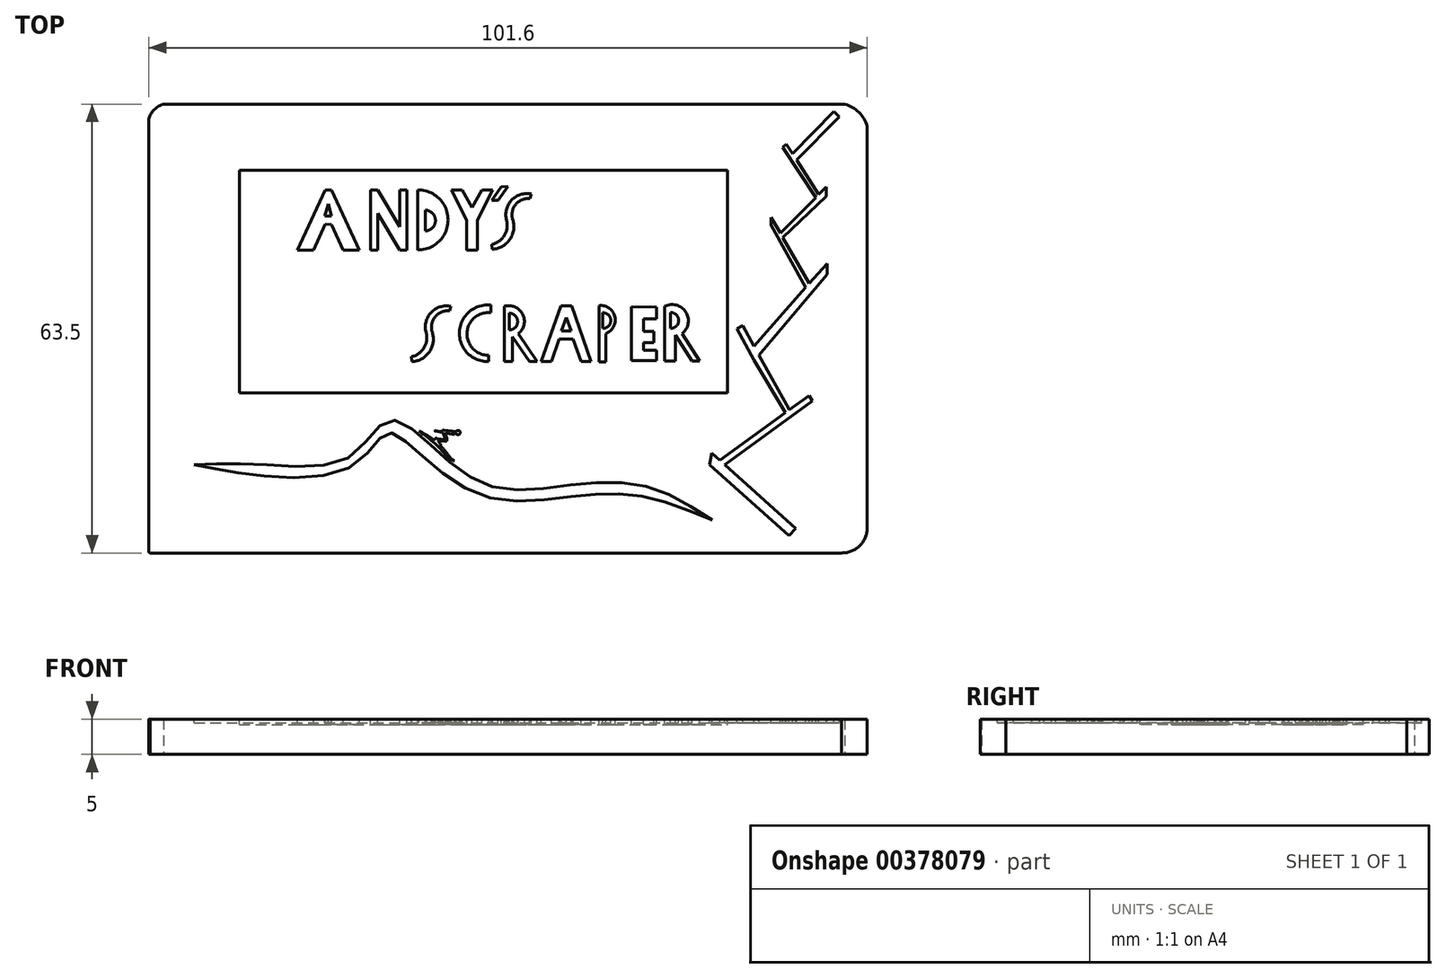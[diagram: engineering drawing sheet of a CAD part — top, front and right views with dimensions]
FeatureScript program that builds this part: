
annotation { "Feature Type Name" : "Feature", "Feature Type Description" : "" }
export const myFeature = defineFeature(function(context is Context, id is Id, definition is map)
    precondition{}
    {
        {
            var Q0;
            Q0=qCreatedBy(makeId("Top.planeOp"),FACE);
            var sketch = newSketch(context, id + "F0", { "sketchPlane" : qUnion([Q0])});
            skLineSegment(sketch, "E0.bottom", {"start": v(2.1, 0) * mm, "end": v(98.44, 0) * mm});
            skLineSegment(sketch, "E0.top", {"start": v(0.18, -63.5) * mm, "end": v(98.16, -63.5) * mm});
            skLineSegment(sketch, "E0.left", {"start": v(0, -2.1) * mm, "end": v(0, -63.32) * mm});
            skLineSegment(sketch, "E0.right", {"start": v(101.6, -3.16) * mm, "end": v(101.6, -60.06) * mm});
            skArc(sketch, "E1", {"start": v(101.6, -3.16) * mm, "mid": v(100.43, -1.17) * mm, "end": v(98.44, 0) * mm});
            skArc(sketch, "E2", {"start": v(2.1, 0) * mm, "mid": v(0.78, -0.78) * mm, "end": v(0, -2.1) * mm});
            skArc(sketch, "E3", {"start": v(98, -63.5) * mm, "mid": v(100.57, -62.47) * mm, "end": v(101.6, -59.9) * mm});
            skArc(sketch, "E4", {"start": v(0, -63.32) * mm, "mid": v(0.05, -63.45) * mm, "end": v(0.18, -63.5) * mm});
            skPoint(sketch, "E5.start.orphan", {"position": v(1.05, -1.05) * mm});
            skSolve(sketch);
        }
        {
            var Q0;
            Q0 = qSketchRegion(id + "F0", true);
            extrude(context, id + "F1", {"entities" : qUnion([Q0]), "depth" : 5 * mm});
        }
        {
            var Q0;
            Q0=makeQuery(id+"F1.opExtrude","CAP_FACE",FACE,{"disambiguationData":[OSD([sQuery(id+"F0.wireOp",EDGE,"E0.bottom"),sQuery(id+"F0.wireOp",EDGE,"E0.top"),sQuery(id+"F0.wireOp",EDGE,"E0.left"),sQuery(id+"F0.wireOp",EDGE,"E0.right"),sQuery(id+"F0.wireOp",EDGE,"E1"),sQuery(id+"F0.wireOp",EDGE,"E2"),sQuery(id+"F0.wireOp",EDGE,"E3"),sQuery(id+"F0.wireOp",EDGE,"E4")])],"isStart":false});
            var sketch = newSketch(context, id + "F2", { "sketchPlane" : qUnion([Q0])});
            skLineSegment(sketch, "E6", {"start": v(21.04, -20.64) * mm, "end": v(23.28, -20.64) * mm});
            skLineSegment(sketch, "E7", {"start": v(23.28, -20.64) * mm, "end": v(24.96, -17) * mm});
            skLineSegment(sketch, "E8", {"start": v(21.04, -20.64) * mm, "end": v(24.96, -12.15) * mm});
            skLineSegment(sketch, "E9", {"start": v(24.9, -15.5) * mm, "end": v(25.4, -15.5) * mm});
            skLineSegment(sketch, "E10", {"start": v(24.9, -15.5) * mm, "end": v(25.4, -13.88) * mm});
            skLineSegment(sketch, "E11.MirrorCS", {"start": v(29.76, -20.69) * mm, "end": v(25.84, -12.15) * mm});
            skLineSegment(sketch, "E12.MirrorCS", {"start": v(27.52, -20.69) * mm, "end": v(25.84, -17.05) * mm});
            skLineSegment(sketch, "E13.MirrorCS", {"start": v(29.76, -20.69) * mm, "end": v(27.52, -20.69) * mm});
            skLineSegment(sketch, "E14.MirrorCS", {"start": v(25.9, -15.5) * mm, "end": v(25.4, -15.5) * mm});
            skLineSegment(sketch, "E15.MirrorCS", {"start": v(25.9, -15.5) * mm, "end": v(25.4, -13.88) * mm});
            skLineSegment(sketch, "E16", {"start": v(31.39, -20.69) * mm, "end": v(31.39, -12.15) * mm});
            skLineSegment(sketch, "E17", {"start": v(31.39, -12.15) * mm, "end": v(32.4, -12.15) * mm});
            skLineSegment(sketch, "E18", {"start": v(36.53, -20.69) * mm, "end": v(35.52, -20.69) * mm});
            skLineSegment(sketch, "E19", {"start": v(32.4, -15.46) * mm, "end": v(32.4, -20.69) * mm});
            skLineSegment(sketch, "E20", {"start": v(32.4, -20.69) * mm, "end": v(31.39, -20.69) * mm});
            skLineSegment(sketch, "E21", {"start": v(35.52, -20.69) * mm, "end": v(36.53, -20.69) * mm});
            skLineSegment(sketch, "E22", {"start": v(36.53, -12.15) * mm, "end": v(36.53, -20.69) * mm});
            skLineSegment(sketch, "E23", {"start": v(36.53, -12.15) * mm, "end": v(35.52, -12.15) * mm});
            skLineSegment(sketch, "E24", {"start": v(35.52, -12.15) * mm, "end": v(35.52, -17.35) * mm});
            skLineSegment(sketch, "E25", {"start": v(32.4, -12.15) * mm, "end": v(35.52, -17.35) * mm});
            skLineSegment(sketch, "E26", {"start": v(32.4, -15.46) * mm, "end": v(35.52, -20.69) * mm});
            skLineSegment(sketch, "E27", {"start": v(38.03, -12.15) * mm, "end": v(38.03, -20.64) * mm});
            skArc(sketch, "E28", {"start": v(38.03, -20.64) * mm, "mid": v(42.33, -16.4) * mm, "end": v(38.03, -12.15) * mm});
            skPoint(sketch, "E29.endSnap0", {"position": v(42.33, -16.4) * mm});
            skLineSegment(sketch, "E30", {"start": v(39.14, -16.42) * mm, "end": v(39.14, -17.62) * mm});
            skLineSegment(sketch, "E31.MirrorCS", {"start": v(39.14, -16.42) * mm, "end": v(39.14, -15.22) * mm});
            skArc(sketch, "E32", {"start": v(39.14, -17.62) * mm, "mid": v(40.36, -16.42) * mm, "end": v(39.14, -15.22) * mm});
            skLineSegment(sketch, "E33", {"start": v(42.77, -12.15) * mm, "end": v(44.93, -16.4) * mm});
            skLineSegment(sketch, "E34", {"start": v(44.93, -16.4) * mm, "end": v(44.93, -20.64) * mm});
            skLineSegment(sketch, "E35", {"start": v(42.77, -12.15) * mm, "end": v(44.3, -12.15) * mm});
            skLineSegment(sketch, "E36", {"start": v(44.3, -12.15) * mm, "end": v(45.7, -14.62) * mm});
            skLineSegment(sketch, "E37.MirrorCS", {"start": v(46.45, -16.4) * mm, "end": v(46.45, -20.64) * mm});
            skLineSegment(sketch, "E38", {"start": v(44.93, -20.64) * mm, "end": v(46.45, -20.64) * mm});
            skLineSegment(sketch, "E39.MirrorCS", {"start": v(47.1, -12.15) * mm, "end": v(45.7, -14.62) * mm});
            skLineSegment(sketch, "E40.MirrorCS", {"start": v(48.62, -12.15) * mm, "end": v(47.1, -12.15) * mm});
            skLineSegment(sketch, "E41.MirrorCS", {"start": v(48.62, -12.15) * mm, "end": v(46.45, -16.4) * mm});
            skPoint(sketch, "E42.endSnap0", {"position": v(36.02, -20.69) * mm});
            skLineSegment(sketch, "E43", {"start": v(49.84, -11.7) * mm, "end": v(48.5, -13.62) * mm});
            skLineSegment(sketch, "E44", {"start": v(48.5, -13.62) * mm, "end": v(49.4, -13.62) * mm});
            skLineSegment(sketch, "E45", {"start": v(49.4, -13.62) * mm, "end": v(50.79, -11.65) * mm});
            skLineSegment(sketch, "E46", {"start": v(50.79, -11.65) * mm, "end": v(49.84, -11.7) * mm});
            skArc(sketch, "E47", {"start": v(54.1, -12.73) * mm, "mid": v(51.32, -13.59) * mm, "end": v(50.6, -16.4) * mm});
            skArc(sketch, "E48", {"start": v(53.93, -13.36) * mm, "mid": v(51.88, -14.21) * mm, "end": v(51.48, -16.4) * mm});
            skLineSegment(sketch, "E49", {"start": v(54.1, -12.73) * mm, "end": v(53.93, -13.36) * mm});
            skArc(sketch, "E50", {"start": v(48.6, -20.53) * mm, "mid": v(51.06, -19.17) * mm, "end": v(51.48, -16.4) * mm});
            skArc(sketch, "E51", {"start": v(48.53, -19.85) * mm, "mid": v(50.3, -18.57) * mm, "end": v(50.6, -16.4) * mm});
            skLineSegment(sketch, "E52", {"start": v(48.53, -19.85) * mm, "end": v(48.6, -20.53) * mm});
            skArc(sketch, "E53.MirrorCS", {"start": v(42.7, -28.62) * mm, "mid": v(39.94, -29.48) * mm, "end": v(39.22, -32.3) * mm});
            skArc(sketch, "E54.MirrorCS", {"start": v(42.54, -29.25) * mm, "mid": v(40.5, -30.1) * mm, "end": v(40.1, -32.3) * mm});
            skArc(sketch, "E55.MirrorCS", {"start": v(37.22, -36.44) * mm, "mid": v(39.68, -35.07) * mm, "end": v(40.1, -32.3) * mm});
            skArc(sketch, "E56.MirrorCS", {"start": v(37.15, -35.75) * mm, "mid": v(38.93, -34.47) * mm, "end": v(39.22, -32.3) * mm});
            skLineSegment(sketch, "E57.MirrorCS", {"start": v(42.7, -28.62) * mm, "end": v(42.54, -29.25) * mm});
            skLineSegment(sketch, "E58.MirrorCS", {"start": v(37.15, -35.75) * mm, "end": v(37.22, -36.44) * mm});
            skArc(sketch, "E59", {"start": v(48.4, -28.45) * mm, "mid": v(43.93, -32.27) * mm, "end": v(48.08, -36.44) * mm});
            skLineSegment(sketch, "E60", {"start": v(48.08, -36.44) * mm, "end": v(48.08, -35.54) * mm});
            skLineSegment(sketch, "E61", {"start": v(48.4, -28.45) * mm, "end": v(48.4, -29.53) * mm});
            skArc(sketch, "E62", {"start": v(48.4, -29.53) * mm, "mid": v(45.01, -32.36) * mm, "end": v(48.08, -35.54) * mm});
            skLineSegment(sketch, "E63", {"start": v(50.26, -28.62) * mm, "end": v(50.26, -36.44) * mm});
            skLineSegment(sketch, "E64", {"start": v(50.26, -36.44) * mm, "end": v(51.42, -36.44) * mm});
            skLineSegment(sketch, "E65", {"start": v(51.42, -36.44) * mm, "end": v(51.42, -32.9) * mm});
            skLineSegment(sketch, "E66", {"start": v(51.42, -32.9) * mm, "end": v(53.87, -36.44) * mm});
            skLineSegment(sketch, "E67", {"start": v(53.87, -36.44) * mm, "end": v(54.92, -36.44) * mm});
            skArc(sketch, "E68", {"start": v(51.42, -32.09) * mm, "mid": v(52.45, -30.92) * mm, "end": v(51.42, -29.75) * mm});
            skLineSegment(sketch, "E69", {"start": v(51.42, -29.75) * mm, "end": v(51.42, -32.09) * mm});
            skArc(sketch, "E70", {"start": v(52.26, -32.5) * mm, "mid": v(52.88, -29.73) * mm, "end": v(50.26, -28.62) * mm});
            skLineSegment(sketch, "E71", {"start": v(54.92, -36.44) * mm, "end": v(52.26, -32.5) * mm});
            skLineSegment(sketch, "E72", {"start": v(55.52, -36.44) * mm, "end": v(58.29, -28.57) * mm});
            skLineSegment(sketch, "E73", {"start": v(58.29, -28.57) * mm, "end": v(59.05, -28.57) * mm});
            skLineSegment(sketch, "E74", {"start": v(55.52, -36.44) * mm, "end": v(56.94, -36.44) * mm});
            skLineSegment(sketch, "E75", {"start": v(56.94, -36.44) * mm, "end": v(58.06, -33.23) * mm});
            skLineSegment(sketch, "E76", {"start": v(59.05, -30.1) * mm, "end": v(58.5, -32.04) * mm});
            skLineSegment(sketch, "E77.MirrorCS", {"start": v(59.05, -30.1) * mm, "end": v(59.6, -32.04) * mm});
            skLineSegment(sketch, "E78.MirrorCS", {"start": v(59.8, -28.57) * mm, "end": v(59.05, -28.57) * mm});
            skLineSegment(sketch, "E79.MirrorCS", {"start": v(62.58, -36.44) * mm, "end": v(59.8, -28.57) * mm});
            skLineSegment(sketch, "E80.MirrorCS", {"start": v(61.16, -36.44) * mm, "end": v(60.03, -33.23) * mm});
            skLineSegment(sketch, "E81.MirrorCS", {"start": v(62.58, -36.44) * mm, "end": v(61.16, -36.44) * mm});
            skLineSegment(sketch, "E82", {"start": v(58.5, -32.04) * mm, "end": v(59.6, -32.04) * mm});
            skLineSegment(sketch, "E83", {"start": v(60.03, -33.23) * mm, "end": v(58.06, -33.23) * mm});
            skLineSegment(sketch, "E84", {"start": v(63.7, -36.45) * mm, "end": v(63.7, -28.52) * mm});
            skLineSegment(sketch, "E85", {"start": v(63.7, -36.45) * mm, "end": v(64.62, -36.45) * mm});
            skLineSegment(sketch, "E86", {"start": v(64.62, -36.45) * mm, "end": v(64.62, -32.46) * mm});
            skArc(sketch, "E87", {"start": v(64.62, -32.46) * mm, "mid": v(65.91, -30.08) * mm, "end": v(63.7, -28.52) * mm});
            skLineSegment(sketch, "E88", {"start": v(64.49, -31.5) * mm, "end": v(64.49, -29.7) * mm});
            skArc(sketch, "E89", {"start": v(64.49, -31.5) * mm, "mid": v(65.17, -30.6) * mm, "end": v(64.49, -29.7) * mm});
            skLineSegment(sketch, "E90", {"start": v(68.27, -28.69) * mm, "end": v(68.27, -36.28) * mm});
            skLineSegment(sketch, "E91", {"start": v(68.27, -36.28) * mm, "end": v(71.83, -36.28) * mm});
            skLineSegment(sketch, "E92", {"start": v(71.83, -36.28) * mm, "end": v(71.83, -34.86) * mm});
            skLineSegment(sketch, "E93", {"start": v(71.83, -34.86) * mm, "end": v(69.95, -34.86) * mm});
            skLineSegment(sketch, "E94", {"start": v(69.95, -34.86) * mm, "end": v(69.95, -33.72) * mm});
            skLineSegment(sketch, "E95", {"start": v(69.95, -33.72) * mm, "end": v(71.41, -33.72) * mm});
            skLineSegment(sketch, "E96", {"start": v(71.41, -33.72) * mm, "end": v(71.41, -32.17) * mm});
            skLineSegment(sketch, "E97", {"start": v(71.41, -32.17) * mm, "end": v(69.99, -32.17) * mm});
            skLineSegment(sketch, "E98", {"start": v(69.99, -32.17) * mm, "end": v(69.99, -30.36) * mm});
            skLineSegment(sketch, "E99", {"start": v(69.99, -30.36) * mm, "end": v(71.83, -30.36) * mm});
            skLineSegment(sketch, "E100", {"start": v(71.83, -30.36) * mm, "end": v(71.83, -28.73) * mm});
            skLineSegment(sketch, "E101", {"start": v(71.83, -28.73) * mm, "end": v(68.27, -28.69) * mm});
            skLineSegment(sketch, "E102", {"start": v(72.96, -36.35) * mm, "end": v(72.96, -28.62) * mm});
            skLineSegment(sketch, "E103", {"start": v(72.96, -36.35) * mm, "end": v(74.5, -36.35) * mm});
            skLineSegment(sketch, "E104", {"start": v(74.5, -36.35) * mm, "end": v(74.5, -32.67) * mm});
            skLineSegment(sketch, "E105", {"start": v(74.5, -32.67) * mm, "end": v(76.82, -36.35) * mm});
            skLineSegment(sketch, "E106", {"start": v(76.82, -36.35) * mm, "end": v(77.91, -36.35) * mm});
            skLineSegment(sketch, "E107", {"start": v(77.91, -36.35) * mm, "end": v(75.47, -32.47) * mm});
            skArc(sketch, "E108", {"start": v(75.47, -32.47) * mm, "mid": v(75.94, -29.42) * mm, "end": v(72.96, -28.62) * mm});
            skLineSegment(sketch, "E109", {"start": v(73.93, -29.42) * mm, "end": v(73.93, -31.42) * mm});
            skArc(sketch, "E110", {"start": v(73.93, -31.42) * mm, "mid": v(74.93, -30.42) * mm, "end": v(73.93, -29.42) * mm});
            skLineSegment(sketch, "E111.bottom", {"start": v(12.82, -9.34) * mm, "end": v(81.83, -9.34) * mm});
            skLineSegment(sketch, "E111.top", {"start": v(12.82, -40.88) * mm, "end": v(81.83, -40.88) * mm});
            skLineSegment(sketch, "E111.left", {"start": v(12.82, -9.34) * mm, "end": v(12.82, -40.88) * mm});
            skLineSegment(sketch, "E111.right", {"start": v(81.83, -9.34) * mm, "end": v(81.83, -40.88) * mm});
            skLineSegment(sketch, "E112", {"start": v(24.96, -17) * mm, "end": v(25.84, -17.05) * mm});
            skLineSegment(sketch, "E113", {"start": v(24.96, -12.15) * mm, "end": v(25.84, -12.15) * mm});
            skSolve(sketch);
        }
        {
            var Q0;
            Q0=makeQuery(id+"F2.imprint","IMPRINT",FACE,{"disambiguationData":[TD([[makeQuery(id+"F2.imprint","IMPRINT",EDGE,{"derivedFrom":sQuery(id+"F2.wireOp",EDGE,"E6")}),-1.0]])]});
            extrude(context, id + "F3", {"entities" : qUnion([Q0]), "operationType" : NewBodyOperationType.REMOVE, "oppositeDirection" : true, "depth" : 0.76 * mm});
        }
        {
            var Q0;
            {var subQ0=sQuery(id+"F0.wireOp",EDGE,"E0.bottom");var subQ1=sQuery(id+"F0.wireOp",EDGE,"E4");var subQ2=sQuery(id+"F0.wireOp",EDGE,"E3");var subQ3=sQuery(id+"F0.wireOp",EDGE,"E2");var subQ4=sQuery(id+"F0.wireOp",EDGE,"E1");var subQ5=sQuery(id+"F0.wireOp",EDGE,"E0.right");var subQ6=sQuery(id+"F0.wireOp",EDGE,"E0.top");var subQ7=sQuery(id+"F0.wireOp",EDGE,"E0.left");Q0=makeQuery(id+"F3.boolean.opBoolean","SPLIT",FACE,{"disambiguationData":[TD([makeQuery(id+"F1.opExtrude","SWEPT_FACE",FACE,{"disambiguationData":[OSD([subQ0])]})])],"derivedFrom":makeQuery(id+"F1.opExtrude","CAP_FACE",FACE,{"disambiguationData":[OSD([subQ0,subQ6,subQ7,subQ5,subQ4,subQ3,subQ2,subQ1])],"isStart":false})});}
            var sketch = newSketch(context, id + "F4", { "sketchPlane" : qUnion([Q0])});
            skLineSegment(sketch, "E114", {"start": v(25.39, -14.1) * mm, "end": v(24.9, -15.86) * mm});
            skLineSegment(sketch, "E115", {"start": v(24.9, -15.86) * mm, "end": v(25.82, -15.86) * mm});
            skLineSegment(sketch, "E116", {"start": v(25.82, -15.86) * mm, "end": v(25.39, -14.1) * mm});
            skLineSegment(sketch, "E117", {"start": v(39.08, -15.02) * mm, "end": v(39.08, -17.95) * mm});
            skArc(sketch, "E118", {"start": v(39.08, -17.95) * mm, "mid": v(40.55, -16.48) * mm, "end": v(39.08, -15.02) * mm});
            skLineSegment(sketch, "E119", {"start": v(50.97, -29.6) * mm, "end": v(50.97, -31.96) * mm});
            skArc(sketch, "E120", {"start": v(50.97, -31.96) * mm, "mid": v(52.17, -30.77) * mm, "end": v(50.97, -29.6) * mm});
            skLineSegment(sketch, "E121", {"start": v(58.33, -32.1) * mm, "end": v(59.72, -32.13) * mm});
            skLineSegment(sketch, "E122", {"start": v(59.06, -30.18) * mm, "end": v(58.33, -32.1) * mm});
            skLineSegment(sketch, "E123", {"start": v(59.06, -30.18) * mm, "end": v(59.72, -32.13) * mm});
            skLineSegment(sketch, "E124", {"start": v(64.22, -29.52) * mm, "end": v(64.22, -31.73) * mm});
            skArc(sketch, "E125", {"start": v(64.22, -31.73) * mm, "mid": v(65.34, -30.63) * mm, "end": v(64.22, -29.52) * mm});
            skLineSegment(sketch, "E126", {"start": v(73.81, -29.5) * mm, "end": v(73.81, -31.74) * mm});
            skArc(sketch, "E127", {"start": v(73.81, -31.74) * mm, "mid": v(74.96, -30.61) * mm, "end": v(73.81, -29.5) * mm});
            skSolve(sketch);
        }
        {
            var Q0;
            Q0 = qSketchRegion(id + "F4", true);
            extrude(context, id + "F5", {"entities" : qUnion([Q0]), "operationType" : NewBodyOperationType.REMOVE, "oppositeDirection" : true, "depth" : 0.5 * mm});
        }
        {
            var Q0;
            {var subQ0=sQuery(id+"F0.wireOp",EDGE,"E0.bottom");var subQ1=sQuery(id+"F0.wireOp",EDGE,"E4");var subQ2=sQuery(id+"F0.wireOp",EDGE,"E3");var subQ3=sQuery(id+"F0.wireOp",EDGE,"E2");var subQ4=sQuery(id+"F0.wireOp",EDGE,"E1");var subQ5=sQuery(id+"F0.wireOp",EDGE,"E0.right");var subQ6=sQuery(id+"F0.wireOp",EDGE,"E0.top");var subQ7=sQuery(id+"F0.wireOp",EDGE,"E0.left");Q0=makeQuery(id+"F3.boolean.opBoolean","SPLIT",FACE,{"disambiguationData":[TD([makeQuery(id+"F1.opExtrude","SWEPT_FACE",FACE,{"disambiguationData":[OSD([subQ0])]})])],"derivedFrom":makeQuery(id+"F1.opExtrude","CAP_FACE",FACE,{"disambiguationData":[OSD([subQ0,subQ6,subQ7,subQ5,subQ4,subQ3,subQ2,subQ1])],"isStart":false})});}
            var sketch = newSketch(context, id + "F6", { "sketchPlane" : qUnion([Q0])});
            skLineSegment(sketch, "E128", {"start": v(85.59, -36.24) * mm, "end": v(83.2, -31.76) * mm});
            skLineSegment(sketch, "E129", {"start": v(83.2, -31.76) * mm, "end": v(84.02, -31.32) * mm});
            skLineSegment(sketch, "E130", {"start": v(84.02, -31.32) * mm, "end": v(85.59, -34.27) * mm});
            skLineSegment(sketch, "E131", {"start": v(85.59, -34.27) * mm, "end": v(92.92, -25.97) * mm});
            skPoint(sketch, "E131.startSnap0", {"position": v(85.59, -36.24) * mm});
            skLineSegment(sketch, "E132", {"start": v(95.95, -22.55) * mm, "end": v(95.95, -24.1) * mm});
            skLineSegment(sketch, "E133", {"start": v(95.95, -24.1) * mm, "end": v(86.27, -35.55) * mm});
            skLineSegment(sketch, "E134", {"start": v(85.59, -36.24) * mm, "end": v(90.05, -43.66) * mm});
            skLineSegment(sketch, "E135", {"start": v(90.57, -43.13) * mm, "end": v(86.27, -35.55) * mm});
            skLineSegment(sketch, "E136", {"start": v(93.44, -25.39) * mm, "end": v(89.68, -18.9) * mm});
            skLineSegment(sketch, "E137", {"start": v(88, -16.03) * mm, "end": v(88, -17.13) * mm});
            skLineSegment(sketch, "E138", {"start": v(88, -17.13) * mm, "end": v(92.92, -25.97) * mm});
            skLineSegment(sketch, "E139", {"start": v(89.32, -18.28) * mm, "end": v(94.33, -13.24) * mm});
            skLineSegment(sketch, "E140", {"start": v(95.82, -11.74) * mm, "end": v(95.82, -13.05) * mm});
            skLineSegment(sketch, "E141", {"start": v(95.82, -13.05) * mm, "end": v(89.68, -18.9) * mm});
            skLineSegment(sketch, "E142", {"start": v(94.74, -12.82) * mm, "end": v(91.62, -7.94) * mm});
            skLineSegment(sketch, "E143", {"start": v(90.17, -5.66) * mm, "end": v(89.68, -6.16) * mm});
            skLineSegment(sketch, "E144", {"start": v(89.68, -6.16) * mm, "end": v(94.33, -13.24) * mm});
            skLineSegment(sketch, "E145", {"start": v(91.05, -7.03) * mm, "end": v(96.92, -1.05) * mm});
            skLineSegment(sketch, "E146", {"start": v(96.92, -1.05) * mm, "end": v(97.67, -1.79) * mm});
            skLineSegment(sketch, "E147", {"start": v(97.67, -1.79) * mm, "end": v(91.62, -7.94) * mm});
            skLineSegment(sketch, "E148", {"start": v(93.39, -41.25) * mm, "end": v(80.74, -50.39) * mm});
            skLineSegment(sketch, "E149", {"start": v(81.46, -51.03) * mm, "end": v(81.46, -51.03) * mm});
            skLineSegment(sketch, "E150", {"start": v(81.46, -51.03) * mm, "end": v(93.83, -41.99) * mm});
            skLineSegment(sketch, "E151", {"start": v(93.83, -41.99) * mm, "end": v(93.39, -41.25) * mm});
            skLineSegment(sketch, "E152", {"start": v(79.62, -49.38) * mm, "end": v(80.74, -50.39) * mm});
            skLineSegment(sketch, "E153", {"start": v(91.5, -60.03) * mm, "end": v(90.57, -61.08) * mm});
            skLineSegment(sketch, "E154", {"start": v(90.57, -61.08) * mm, "end": v(79.34, -51.03) * mm});
            skLineSegment(sketch, "E155", {"start": v(79.34, -51.03) * mm, "end": v(79.62, -49.38) * mm});
            skLineSegment(sketch, "E156.trimOffspring", {"start": v(81.46, -51.03) * mm, "end": v(91.5, -60.03) * mm});
            skLineSegment(sketch, "E157.trimOffspring", {"start": v(90.57, -43.3) * mm, "end": v(90.57, -43.13) * mm});
            skPoint(sketch, "E158.trimOffspring.end.orphan", {"position": v(90.57, -44.52) * mm});
            skLineSegment(sketch, "E159.trimOffspring", {"start": v(93.44, -25.39) * mm, "end": v(95.95, -22.55) * mm});
            skLineSegment(sketch, "E160.trimOffspring", {"start": v(89.32, -18.28) * mm, "end": v(88, -16.03) * mm});
            skLineSegment(sketch, "E161.trimOffspring", {"start": v(94.74, -12.82) * mm, "end": v(95.82, -11.74) * mm});
            skLineSegment(sketch, "E162.trimOffspring", {"start": v(91.05, -7.03) * mm, "end": v(90.17, -5.66) * mm});
            skSolve(sketch);
        }
        {
            var Q0;
            Q0 = qSketchRegion(id + "F6", true);
            extrude(context, id + "F7", {"entities" : qUnion([Q0]), "operationType" : NewBodyOperationType.REMOVE, "oppositeDirection" : true, "depth" : 0.5 * mm});
        }
        {
            var Q0;
            {var subQ0=sQuery(id+"F0.wireOp",EDGE,"E0.bottom");var subQ1=sQuery(id+"F0.wireOp",EDGE,"E4");var subQ2=sQuery(id+"F0.wireOp",EDGE,"E3");var subQ3=sQuery(id+"F0.wireOp",EDGE,"E2");var subQ4=sQuery(id+"F0.wireOp",EDGE,"E1");var subQ5=sQuery(id+"F0.wireOp",EDGE,"E0.right");var subQ6=sQuery(id+"F0.wireOp",EDGE,"E0.top");var subQ7=sQuery(id+"F0.wireOp",EDGE,"E0.left");Q0=makeQuery(id+"F3.boolean.opBoolean","SPLIT",FACE,{"disambiguationData":[TD([makeQuery(id+"F1.opExtrude","SWEPT_FACE",FACE,{"disambiguationData":[OSD([subQ0])]})])],"derivedFrom":makeQuery(id+"F1.opExtrude","CAP_FACE",FACE,{"disambiguationData":[OSD([subQ0,subQ6,subQ7,subQ5,subQ4,subQ3,subQ2,subQ1])],"isStart":false})});}
            var sketch = newSketch(context, id + "F8", { "sketchPlane" : qUnion([Q0])});
            skFitSpline(sketch, "E163", {"points": [v(6.42, -51) * mm, v(16.15, -51) * mm, v(28.4, -49.9) * mm, v(33.88, -44.74) * mm, v(39.9, -48.29) * mm, v(48.5, -54.1) * mm, v(59.9, -53.88) * mm, v(70.42, -54.1) * mm, v(79.67, -58.82) * mm], "startDerivative": vector(72.85, 2.56) * mm, "endDerivative": vector(69.96, -45.11) * mm});
            skFitSpline(sketch, "E164", {"points": [v(6.42, -51) * mm, v(15.83, -52.59) * mm, v(29.15, -51) * mm, v(33.67, -46.57) * mm, v(37.86, -49.04) * mm, v(47.75, -55.6) * mm, v(60.1, -55.49) * mm, v(69.67, -55.49) * mm, v(79.67, -58.82) * mm], "startDerivative": vector(68.22, -14.71) * mm, "endDerivative": vector(77.09, -31.4) * mm});
            skSolve(sketch);
        }
        {
            var Q0;
            Q0 = qSketchRegion(id + "F8", true);
            extrude(context, id + "F9", {"entities" : qUnion([Q0]), "operationType" : NewBodyOperationType.REMOVE, "oppositeDirection" : true, "depth" : 0.5 * mm});
        }
        {
            var Q0;
            {var subQ0=sQuery(id+"F0.wireOp",EDGE,"E0.bottom");var subQ1=sQuery(id+"F0.wireOp",EDGE,"E4");var subQ2=sQuery(id+"F0.wireOp",EDGE,"E3");var subQ3=sQuery(id+"F0.wireOp",EDGE,"E2");var subQ4=sQuery(id+"F0.wireOp",EDGE,"E1");var subQ5=sQuery(id+"F0.wireOp",EDGE,"E0.right");var subQ6=sQuery(id+"F0.wireOp",EDGE,"E0.top");var subQ7=sQuery(id+"F0.wireOp",EDGE,"E0.left");Q0=makeQuery(id+"F3.boolean.opBoolean","SPLIT",FACE,{"disambiguationData":[TD([makeQuery(id+"F1.opExtrude","SWEPT_FACE",FACE,{"disambiguationData":[OSD([subQ0])]})])],"derivedFrom":makeQuery(id+"F1.opExtrude","CAP_FACE",FACE,{"disambiguationData":[OSD([subQ0,subQ6,subQ7,subQ5,subQ4,subQ3,subQ2,subQ1])],"isStart":false})});}
            var sketch = newSketch(context, id + "F10", { "sketchPlane" : qUnion([Q0])});
            skArc(sketch, "E165", {"start": v(42.42, -50.13) * mm, "mid": v(40.48, -48.05) * mm, "end": v(38.26, -46.29) * mm});
            skArc(sketch, "E166", {"start": v(42.42, -50.13) * mm, "mid": v(42.8, -50.35) * mm, "end": v(43.23, -50.45) * mm});
            skArc(sketch, "E167", {"start": v(42.6, -49.97) * mm, "mid": v(41.95, -49.11) * mm, "end": v(41.23, -48.33) * mm});
            skArc(sketch, "E168", {"start": v(42.6, -49.97) * mm, "mid": v(42.89, -50.24) * mm, "end": v(43.23, -50.45) * mm});
            skLineSegment(sketch, "E169", {"start": v(40.31, -47.53) * mm, "end": v(40.49, -47.31) * mm});
            skLineSegment(sketch, "E170", {"start": v(41.97, -47.39) * mm, "end": v(41.57, -46.46) * mm});
            skLineSegment(sketch, "E171", {"start": v(41.75, -46.13) * mm, "end": v(43.5, -46.32) * mm});
            skLineSegment(sketch, "E172", {"start": v(41.98, -47.7) * mm, "end": v(41.04, -47.63) * mm});
            skLineSegment(sketch, "E173", {"start": v(40.95, -47.7) * mm, "end": v(41.22, -48.03) * mm});
            skArc(sketch, "E174", {"start": v(41.23, -48.33) * mm, "mid": v(41.28, -48.18) * mm, "end": v(41.22, -48.03) * mm});
            skLineSegment(sketch, "E175", {"start": v(40.81, -47.31) * mm, "end": v(41.88, -47.48) * mm});
            skArc(sketch, "E176", {"start": v(41.75, -46.13) * mm, "mid": v(41.6, -46.16) * mm, "end": v(41.48, -46.25) * mm});
            skArc(sketch, "E177", {"start": v(41.88, -47.48) * mm, "mid": v(41.95, -47.46) * mm, "end": v(41.97, -47.39) * mm});
            skArc(sketch, "E178", {"start": v(41.98, -47.7) * mm, "mid": v(42.1, -47.67) * mm, "end": v(42.18, -47.56) * mm});
            skArc(sketch, "E179", {"start": v(40.81, -47.31) * mm, "mid": v(40.65, -47.3) * mm, "end": v(40.49, -47.31) * mm});
            skArc(sketch, "E180", {"start": v(41.04, -47.63) * mm, "mid": v(40.98, -47.65) * mm, "end": v(40.95, -47.7) * mm});
            skLineSegment(sketch, "E181", {"start": v(43.53, -46.67) * mm, "end": v(43.5, -46.67) * mm});
            skFitSpline(sketch, "E182", {"points": [v(42.18, -47.56) * mm, v(42.18, -47.4) * mm, v(42.07, -46.96) * mm, v(41.95, -46.63) * mm, v(42.15, -46.58) * mm], "startDerivative": vector(0.04, 0.71) * mm, "endDerivative": vector(1.2, 0.05) * mm});
            skArc(sketch, "E183", {"start": v(43.53, -46.67) * mm, "mid": v(44.04, -46.44) * mm, "end": v(43.5, -46.32) * mm});
            skFitSpline(sketch, "E184", {"points": [v(43.43, -46.58) * mm, v(43.45, -46.84) * mm, v(44.01, -47.07) * mm, v(44.66, -47) * mm, v(44.76, -47) * mm, v(44.75, -47.08) * mm, v(44.01, -47.22) * mm, v(43.33, -46.96) * mm, v(43.28, -46.6) * mm, v(43.43, -46.58) * mm]});
            skArc(sketch, "E185", {"start": v(43.5, -46.67) * mm, "mid": v(43.45, -46.69) * mm, "end": v(43.43, -46.73) * mm});
            skArc(sketch, "E186", {"start": v(43.24, -46.67) * mm, "mid": v(43.23, -46.66) * mm, "end": v(43.2, -46.65) * mm});
            skLineSegment(sketch, "E187.trimOffspring", {"start": v(43.2, -46.65) * mm, "end": v(42.83, -46.62) * mm});
            skLineSegment(sketch, "E188", {"start": v(44.88, -47) * mm, "end": v(43.43, -46.74) * mm});
            skLineSegment(sketch, "E189", {"start": v(42.22, -46.58) * mm, "end": v(43.25, -46.78) * mm});
            skLineSegment(sketch, "E190", {"start": v(44.84, -47.08) * mm, "end": v(44.88, -47) * mm});
            skArc(sketch, "E191", {"start": v(40.49, -46.3) * mm, "mid": v(40.5, -46.28) * mm, "end": v(40.52, -46.25) * mm});
            skPoint(sketch, "E192.start.orphan", {"position": v(40.53, -46.23) * mm});
            skLineSegment(sketch, "E193", {"start": v(41.54, -46.38) * mm, "end": v(40.54, -46.2) * mm});
            skLineSegment(sketch, "E194", {"start": v(41.57, -46.46) * mm, "end": v(40.52, -46.25) * mm});
            skArc(sketch, "E195", {"start": v(40.49, -46.3) * mm, "mid": v(40.5, -46.27) * mm, "end": v(40.51, -46.24) * mm});
            skLineSegment(sketch, "E196", {"start": v(40.53, -46.2) * mm, "end": v(40.46, -46.2) * mm});
            skLineSegment(sketch, "E197", {"start": v(40.46, -46.2) * mm, "end": v(40.51, -46.24) * mm});
            skArc(sketch, "E198.trimOffspring", {"start": v(40.53, -46.2) * mm, "mid": v(40.53, -46.17) * mm, "end": v(40.54, -46.14) * mm});
            skArc(sketch, "E199.trimOffspring", {"start": v(40.54, -46.2) * mm, "mid": v(40.54, -46.17) * mm, "end": v(40.54, -46.14) * mm});
            skLineSegment(sketch, "E200.trimOffspring", {"start": v(41.54, -46.38) * mm, "end": v(41.48, -46.25) * mm});
            skLineSegment(sketch, "E201.trimOffspring", {"start": v(42.22, -46.58) * mm, "end": v(42.15, -46.58) * mm});
            skArc(sketch, "E202.trimOffspring", {"start": v(40.31, -47.53) * mm, "mid": v(39.32, -46.85) * mm, "end": v(38.26, -46.29) * mm});
            skLineSegment(sketch, "E203.trimOffspring", {"start": v(43.24, -46.7) * mm, "end": v(42.83, -46.62) * mm});
            skLineSegment(sketch, "E204.trimOffspring", {"start": v(43.44, -46.82) * mm, "end": v(44.52, -47.02) * mm});
            skLineSegment(sketch, "E205.trimOffspring", {"start": v(44.76, -47.07) * mm, "end": v(44.84, -47.08) * mm});
            skSolve(sketch);
        }
        {
            var Q0;
            Q0=makeQuery(id+"F10.imprint","IMPRINT",FACE,{"disambiguationData":[TD([[makeQuery(id+"F10.imprint","IMPRINT",EDGE,{"derivedFrom":sQuery(id+"F10.wireOp",EDGE,"E165")}),-1.0]])]});
            extrude(context, id + "F11", {"entities" : qUnion([Q0]), "operationType" : NewBodyOperationType.REMOVE, "oppositeDirection" : true, "depth" : 0.5 * mm});
        }
    });
